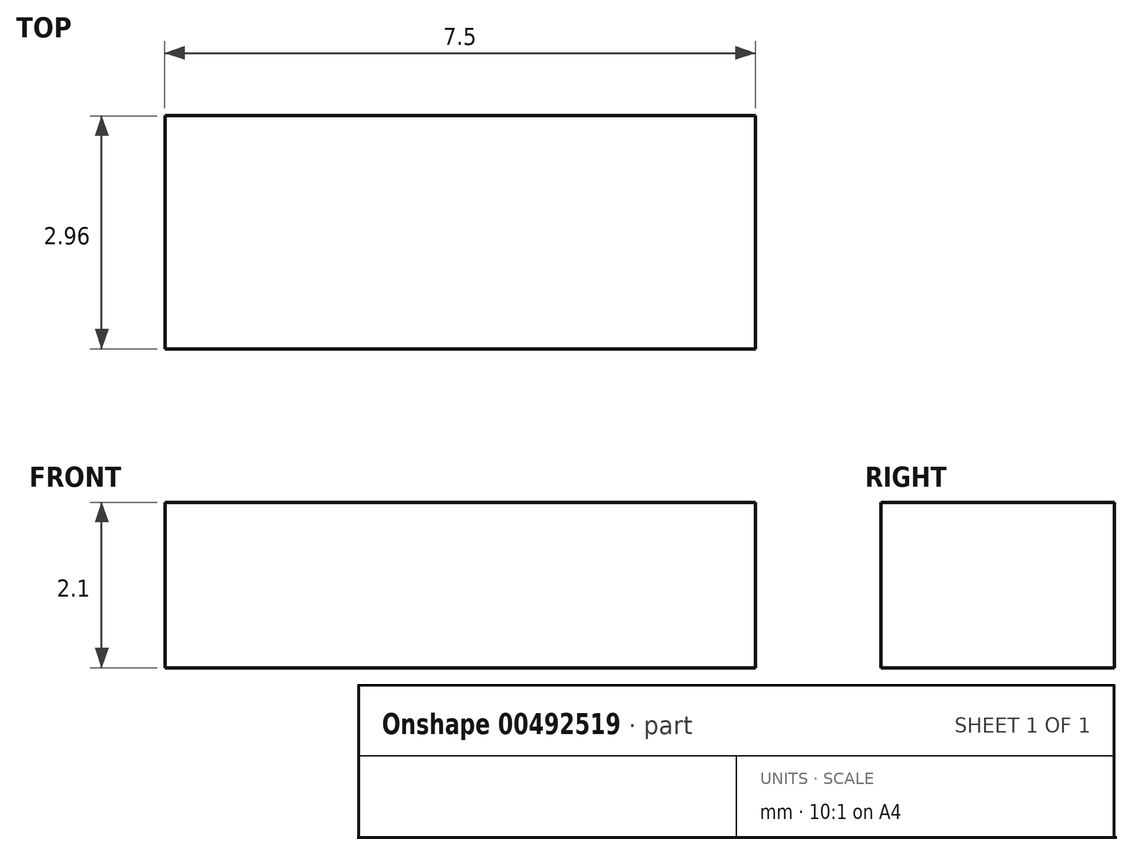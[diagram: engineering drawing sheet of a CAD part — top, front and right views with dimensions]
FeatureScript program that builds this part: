
annotation { "Feature Type Name" : "Feature", "Feature Type Description" : "" }
export const myFeature = defineFeature(function(context is Context, id is Id, definition is map)
    precondition{}
    {
        {
            var Q0;
            Q0=qCreatedBy(makeId("Top.planeOp"),FACE);
            var sketch = newSketch(context, id + "F0", { "sketchPlane" : qUnion([Q0])});
            skLineSegment(sketch, "E0.bottom", {"start": v(-40.4, 19.15) * mm, "end": v(-32.9, 19.15) * mm});
            skLineSegment(sketch, "E0.top", {"start": v(-40.4, 16.19) * mm, "end": v(-32.9, 16.19) * mm});
            skLineSegment(sketch, "E0.left", {"start": v(-40.4, 19.15) * mm, "end": v(-40.4, 16.19) * mm});
            skLineSegment(sketch, "E0.right", {"start": v(-32.9, 19.15) * mm, "end": v(-32.9, 16.19) * mm});
            skSolve(sketch);
        }
        {
            var Q0;
            Q0=makeQuery(id+"F0.imprint","IMPRINT",FACE,{"disambiguationData":[TD([[makeQuery(id+"F0.imprint","IMPRINT",EDGE,{"derivedFrom":sQuery(id+"F0.wireOp",EDGE,"E0.bottom")}),-1.0]])]});
            extrude(context, id + "F1", {"entities" : qUnion([Q0]), "depth" : 2.1 * mm});
        }
    });
